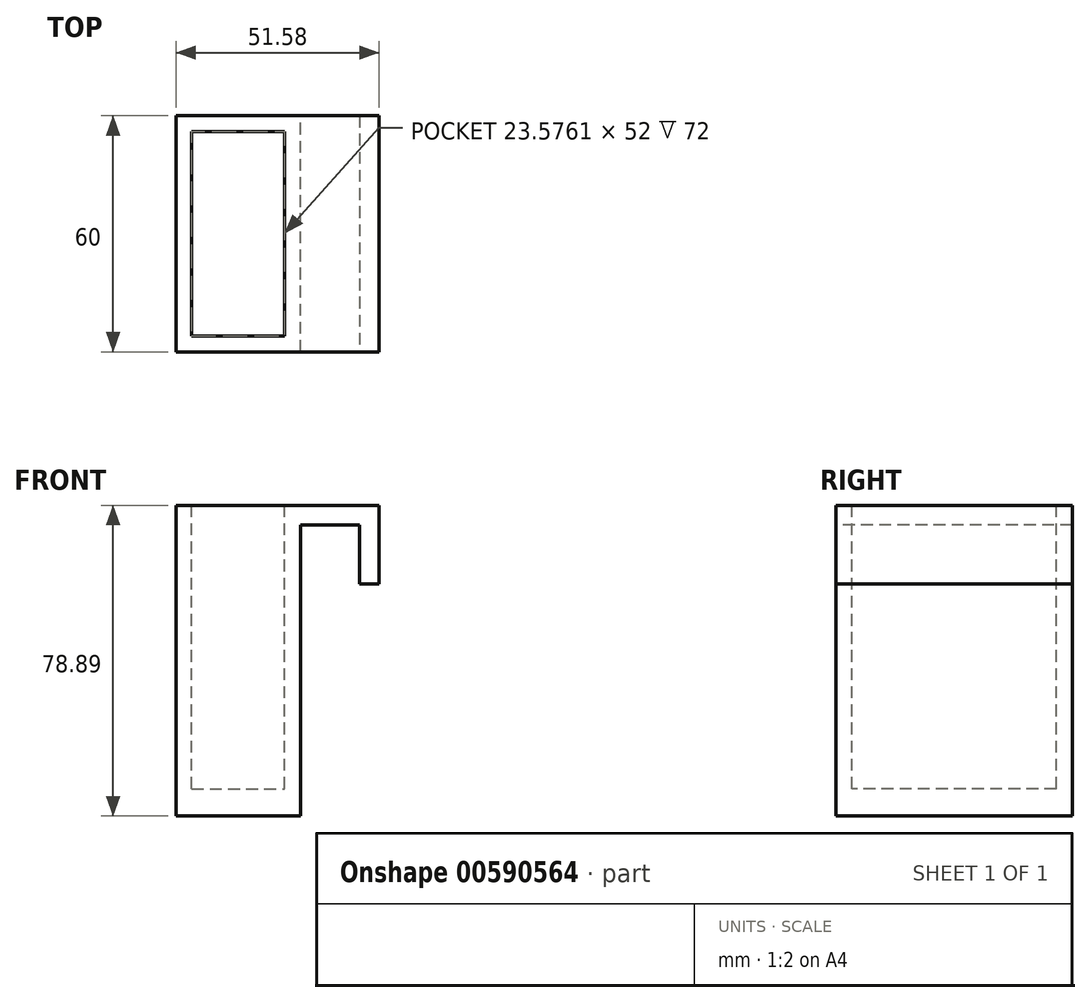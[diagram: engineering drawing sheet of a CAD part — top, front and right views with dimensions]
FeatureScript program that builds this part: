
annotation { "Feature Type Name" : "Feature", "Feature Type Description" : "" }
export const myFeature = defineFeature(function(context is Context, id is Id, definition is map)
    precondition{}
    {
        {
            var Q0;
            Q0=qCreatedBy(makeId("Front.planeOp"),FACE);
            var sketch = newSketch(context, id + "F0", { "sketchPlane" : qUnion([Q0])});
            skLineSegment(sketch, "E0.bottom", {"start": v(0, 0) * mm, "end": v(31.58, 0) * mm});
            skLineSegment(sketch, "E0.top", {"start": v(0, 78.9) * mm, "end": v(31.58, 78.9) * mm});
            skLineSegment(sketch, "E0.left", {"start": v(0, 0) * mm, "end": v(0, 78.9) * mm});
            skLineSegment(sketch, "E0.right", {"start": v(31.58, 0) * mm, "end": v(31.58, 78.9) * mm});
            skSolve(sketch);
        }
        {
            var Q0;
            Q0 = qSketchRegion(id + "F0", true);
            extrude(context, id + "F1", {"entities" : qUnion([Q0]), "depth" : 60 * mm, "offsetDistance" : 25 * mm});
        }
        {
            var Q0;
            Q0=makeQuery(id+"F1.opExtrude","SWEPT_FACE",FACE,{"disambiguationData":[OSD([sQuery(id+"F0.wireOp",EDGE,"E0.top")])]});
            var sketch = newSketch(context, id + "F2", { "sketchPlane" : qUnion([Q0])});
            skLineSegment(sketch, "E1.bottom", {"start": v(4, -4) * mm, "end": v(27.58, -4) * mm});
            skLineSegment(sketch, "E1.top", {"start": v(4, -56) * mm, "end": v(27.58, -56) * mm});
            skLineSegment(sketch, "E1.left", {"start": v(4, -4) * mm, "end": v(4, -56) * mm});
            skLineSegment(sketch, "E1.right", {"start": v(27.58, -4) * mm, "end": v(27.58, -56) * mm});
            skLineSegment(sketch, "E2", {"start": v(27.58, -56) * mm, "end": v(27.58, -60) * mm, "construction": true});
            skPoint(sketch, "E2.endSnap0", {"position": v(15.79, -60) * mm});
            skLineSegment(sketch, "E3", {"start": v(27.58, -4) * mm, "end": v(27.58, 0) * mm, "construction": true});
            skLineSegment(sketch, "E4", {"start": v(4, -4) * mm, "end": v(0, -4) * mm, "construction": true});
            skLineSegment(sketch, "E5", {"start": v(27.58, -4) * mm, "end": v(31.58, -4) * mm, "construction": true});
            skSolve(sketch);
        }
        {
            var Q0;
            Q0=makeQuery(id+"F2.imprint","IMPRINT",FACE,{"disambiguationData":[TD([[makeQuery(id+"F2.imprint","IMPRINT",EDGE,{"derivedFrom":sQuery(id+"F2.wireOp",EDGE,"E1.bottom")}),-1.0]])]});
            extrude(context, id + "F3", {"entities" : qUnion([Q0]), "operationType" : NewBodyOperationType.REMOVE, "oppositeDirection" : true, "depth" : 72 * mm, "offsetDistance" : 25 * mm});
        }
        {
            var Q0;
            Q0=makeQuery(id+"F1.opExtrude","CAP_FACE",FACE,{"disambiguationData":[OSD([sQuery(id+"F0.wireOp",EDGE,"E0.bottom"),sQuery(id+"F0.wireOp",EDGE,"E0.top"),sQuery(id+"F0.wireOp",EDGE,"E0.left"),sQuery(id+"F0.wireOp",EDGE,"E0.right")])],"isStart":false});
            var sketch = newSketch(context, id + "F4", { "sketchPlane" : qUnion([Q0])});
            skLineSegment(sketch, "E6", {"start": v(31.58, 78.9) * mm, "end": v(51.58, 78.9) * mm});
            skLineSegment(sketch, "E7", {"start": v(51.58, 78.9) * mm, "end": v(51.58, 58.9) * mm});
            skLineSegment(sketch, "E8", {"start": v(51.58, 58.9) * mm, "end": v(46.58, 58.9) * mm});
            skLineSegment(sketch, "E9", {"start": v(46.58, 58.9) * mm, "end": v(46.58, 73.9) * mm});
            skLineSegment(sketch, "E10", {"start": v(46.58, 73.9) * mm, "end": v(31.58, 73.9) * mm});
            skLineSegment(sketch, "E11", {"start": v(46.58, 73.9) * mm, "end": v(46.58, 78.9) * mm, "construction": true});
            skLineSegment(sketch, "E12", {"start": v(31.58, 78.9) * mm, "end": v(31.58, 73.9) * mm});
            skSolve(sketch);
        }
        {
            var Q0;
            Q0 = qSketchRegion(id + "F4", true);
            extrude(context, id + "F5", {"entities" : qUnion([Q0]), "operationType" : NewBodyOperationType.ADD, "oppositeDirection" : true, "depth" : 60 * mm, "offsetDistance" : 25 * mm});
        }
    });
